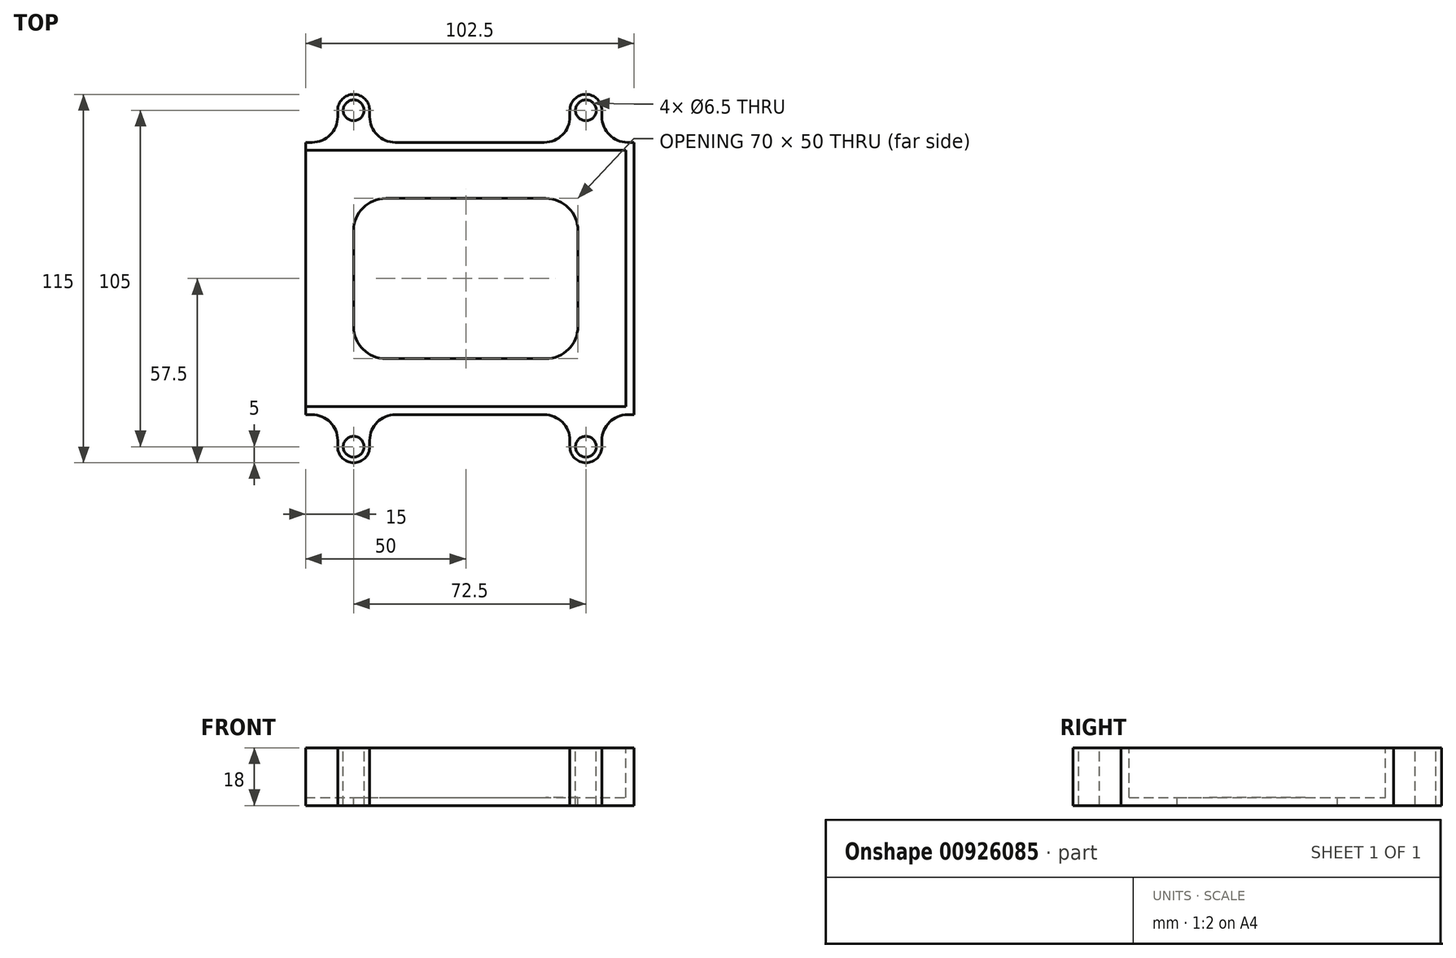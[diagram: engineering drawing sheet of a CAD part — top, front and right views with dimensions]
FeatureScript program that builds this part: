
annotation { "Feature Type Name" : "Feature", "Feature Type Description" : "" }
export const myFeature = defineFeature(function(context is Context, id is Id, definition is map)
    precondition{}
    {
        {
            var Q0;
            Q0=qCreatedBy(makeId("Top.planeOp"),FACE);
            var sketch = newSketch(context, id + "F0", { "sketchPlane" : qUnion([Q0])});
            skLineSegment(sketch, "E0.bottom", {"start": v(-50, -42.5) * mm, "end": v(-40, -42.5) * mm});
            skLineSegment(sketch, "E0.top", {"start": v(-50, 42.5) * mm, "end": v(-40, 42.5) * mm});
            skLineSegment(sketch, "E0.left", {"start": v(-50, -42.5) * mm, "end": v(-50, 42.5) * mm});
            skLineSegment(sketch, "E0.right", {"start": v(52.5, -42.5) * mm, "end": v(52.5, 42.5) * mm});
            skLineSegment(sketch, "E1.left", {"start": v(-40, -42.5) * mm, "end": v(-40, -52.5) * mm});
            skLineSegment(sketch, "E1.right", {"start": v(-30, -42.5) * mm, "end": v(-30, -52.5) * mm});
            skLineSegment(sketch, "E2.left", {"start": v(42.5, -42.5) * mm, "end": v(42.5, -52.5) * mm});
            skLineSegment(sketch, "E2.right", {"start": v(32.5, -42.5) * mm, "end": v(32.5, -52.5) * mm});
            skArc(sketch, "E3", {"start": v(-40, -52.5) * mm, "mid": v(-35, -57.5) * mm, "end": v(-30, -52.5) * mm});
            skArc(sketch, "E4", {"start": v(32.5, -52.5) * mm, "mid": v(37.5, -57.5) * mm, "end": v(42.5, -52.5) * mm});
            skLineSegment(sketch, "E5.trimOffspring", {"start": v(-30, -42.5) * mm, "end": v(32.5, -42.5) * mm});
            skLineSegment(sketch, "E6.trimOffspring", {"start": v(42.5, -42.5) * mm, "end": v(52.5, -42.5) * mm});
            skArc(sketch, "E7.MirrorCS", {"start": v(-40, 52.5) * mm, "mid": v(-35, 57.5) * mm, "end": v(-30, 52.5) * mm});
            skLineSegment(sketch, "E8.MirrorCS", {"start": v(-40, 42.5) * mm, "end": v(-40, 52.5) * mm});
            skLineSegment(sketch, "E9.MirrorCS", {"start": v(42.5, 42.5) * mm, "end": v(42.5, 52.5) * mm});
            skLineSegment(sketch, "E10.MirrorCS", {"start": v(-30, 42.5) * mm, "end": v(-30, 52.5) * mm});
            skArc(sketch, "E11.MirrorCS", {"start": v(32.5, 52.5) * mm, "mid": v(37.5, 57.5) * mm, "end": v(42.5, 52.5) * mm});
            skLineSegment(sketch, "E12.MirrorCS", {"start": v(32.5, 42.5) * mm, "end": v(32.5, 52.5) * mm});
            skLineSegment(sketch, "E13.trimOffspring", {"start": v(-30, 42.5) * mm, "end": v(32.5, 42.5) * mm});
            skLineSegment(sketch, "E14.trimOffspring", {"start": v(42.5, 42.5) * mm, "end": v(52.5, 42.5) * mm});
            skCircle(sketch, "E15", {"center": v(-35, -52.5) * mm, "radius": 3.25 * mm});
            skCircle(sketch, "E16", {"center": v(-35, 52.5) * mm, "radius": 3.25 * mm});
            skCircle(sketch, "E17", {"center": v(37.5, -52.5) * mm, "radius": 3.25 * mm});
            skCircle(sketch, "E18", {"center": v(37.5, 52.5) * mm, "radius": 3.25 * mm});
            skSolve(sketch);
        }
        {
            var Q0;
            Q0=qCreatedBy(makeId("Top.planeOp"),FACE);
            var sketch = newSketch(context, id + "F1", { "sketchPlane" : qUnion([Q0])});
            skLineSegment(sketch, "E19.bottom", {"start": v(-25, 25) * mm, "end": v(25, 25) * mm});
            skLineSegment(sketch, "E19.top", {"start": v(-25, -25) * mm, "end": v(25, -25) * mm});
            skLineSegment(sketch, "E19.left", {"start": v(-35, 15) * mm, "end": v(-35, -15) * mm});
            skLineSegment(sketch, "E19.right", {"start": v(35, 15) * mm, "end": v(35, -15) * mm});
            skPoint(sketch, "E20.visualSharp", {"position": v(-35, 25) * mm});
            skArc(sketch, "E20.filletArc", {"start": v(-25, 25) * mm, "mid": v(-32.07, 22.07) * mm, "end": v(-35, 15) * mm});
            skPoint(sketch, "E21.visualSharp", {"position": v(35, 25) * mm});
            skArc(sketch, "E21.filletArc", {"start": v(35, 15) * mm, "mid": v(32.07, 22.07) * mm, "end": v(25, 25) * mm});
            skPoint(sketch, "E22.visualSharp", {"position": v(35, -25) * mm});
            skArc(sketch, "E22.filletArc", {"start": v(25, -25) * mm, "mid": v(32.07, -22.07) * mm, "end": v(35, -15) * mm});
            skPoint(sketch, "E23.visualSharp", {"position": v(-35, -25) * mm});
            skArc(sketch, "E23.filletArc", {"start": v(-35, -15) * mm, "mid": v(-32.07, -22.07) * mm, "end": v(-25, -25) * mm});
            skSolve(sketch);
        }
        {
            var Q0;
            Q0=makeQuery(id+"F0.imprint","IMPRINT",FACE,{"disambiguationData":[TD([[makeQuery(id+"F0.imprint","IMPRINT",EDGE,{"derivedFrom":sQuery(id+"F0.wireOp",EDGE,"E0.bottom")}),1.0]])]});
            var sketch = newSketch(context, id + "F2", { "sketchPlane" : qUnion([Q0])});
            skLineSegment(sketch, "E24.bottom", {"start": v(-50, 40) * mm, "end": v(50, 40) * mm});
            skLineSegment(sketch, "E24.top", {"start": v(-50, -40) * mm, "end": v(50, -40) * mm});
            skLineSegment(sketch, "E24.left", {"start": v(-50, 40) * mm, "end": v(-50, -40) * mm});
            skLineSegment(sketch, "E24.right", {"start": v(50, 40) * mm, "end": v(50, -40) * mm});
            skSolve(sketch);
        }
        {
            var Q0;
            Q0=makeQuery(id+"F0.imprint","IMPRINT",FACE,{"disambiguationData":[TD([[makeQuery(id+"F0.imprint","IMPRINT",EDGE,{"derivedFrom":sQuery(id+"F0.wireOp",EDGE,"E0.bottom")}),1.0]])]});
            extrude(context, id + "F3", {"entities" : qUnion([Q0]), "depth" : -18 * mm, "offsetDistance" : 25 * mm});
        }
        {
            var Q0;
            Q0=makeQuery(id+"F2.imprint","IMPRINT",FACE,{"disambiguationData":[TD([[makeQuery(id+"F2.imprint","IMPRINT",EDGE,{"derivedFrom":sQuery(id+"F2.wireOp",EDGE,"E24.bottom")}),-1.0]])]});
            extrude(context, id + "F4", {"entities" : qUnion([Q0]), "operationType" : NewBodyOperationType.REMOVE, "oppositeDirection" : true, "depth" : 15.5 * mm, "offsetDistance" : 25 * mm});
        }
        {
            var Q0;
            Q0=makeQuery(id+"F1.imprint","IMPRINT",FACE,{"disambiguationData":[TD([[makeQuery(id+"F1.imprint","IMPRINT",EDGE,{"derivedFrom":sQuery(id+"F1.wireOp",EDGE,"E19.bottom")}),-1.0]])]});
            extrude(context, id + "F5", {"entities" : qUnion([Q0]), "operationType" : NewBodyOperationType.REMOVE, "oppositeDirection" : true, "depth" : 25 * mm, "offsetDistance" : 25 * mm});
        }
        {
            var Q0;
            Q0=makeQuery(id+"F3.opExtrude","SWEPT_EDGE",EDGE,{"disambiguationData":[OSD([sQuery(id+"F0.wireOp",EDGE,"E0.top"),sQuery(id+"F0.wireOp",EDGE,"E8.MirrorCS")])]});
            var Q1;
            Q1=makeQuery(id+"F3.opExtrude","SWEPT_EDGE",EDGE,{"disambiguationData":[OSD([sQuery(id+"F0.wireOp",EDGE,"E12.MirrorCS"),sQuery(id+"F0.wireOp",EDGE,"E13.trimOffspring")])]});
            var Q2;
            Q2=makeQuery(id+"F3.opExtrude","SWEPT_EDGE",EDGE,{"disambiguationData":[OSD([sQuery(id+"F0.wireOp",EDGE,"E0.bottom"),sQuery(id+"F0.wireOp",EDGE,"E1.left")])]});
            var Q3;
            Q3=makeQuery(id+"F3.opExtrude","SWEPT_EDGE",EDGE,{"disambiguationData":[OSD([sQuery(id+"F0.wireOp",EDGE,"E2.right"),sQuery(id+"F0.wireOp",EDGE,"E5.trimOffspring")])]});
            var Q4;
            Q4=makeQuery(id+"F3.opExtrude","SWEPT_EDGE",EDGE,{"disambiguationData":[OSD([sQuery(id+"F0.wireOp",EDGE,"E2.left"),sQuery(id+"F0.wireOp",EDGE,"E6.trimOffspring")])]});
            var Q5;
            Q5=makeQuery(id+"F3.opExtrude","SWEPT_EDGE",EDGE,{"disambiguationData":[OSD([sQuery(id+"F0.wireOp",EDGE,"E1.right"),sQuery(id+"F0.wireOp",EDGE,"E5.trimOffspring")])]});
            var Q6;
            Q6=makeQuery(id+"F3.opExtrude","SWEPT_EDGE",EDGE,{"disambiguationData":[OSD([sQuery(id+"F0.wireOp",EDGE,"E9.MirrorCS"),sQuery(id+"F0.wireOp",EDGE,"E14.trimOffspring")])]});
            var Q7;
            Q7=makeQuery(id+"F3.opExtrude","SWEPT_EDGE",EDGE,{"disambiguationData":[OSD([sQuery(id+"F0.wireOp",EDGE,"E10.MirrorCS"),sQuery(id+"F0.wireOp",EDGE,"E13.trimOffspring")])]});
            fillet(context, id + "F6", {"entities" : qUnion([Q0, Q1, Q2, Q3, Q4, Q5, Q6, Q7]), "radius" : 8 * mm, "tangentPropagation" : true, "allowEdgeOverflow" : false});
        }
    });
